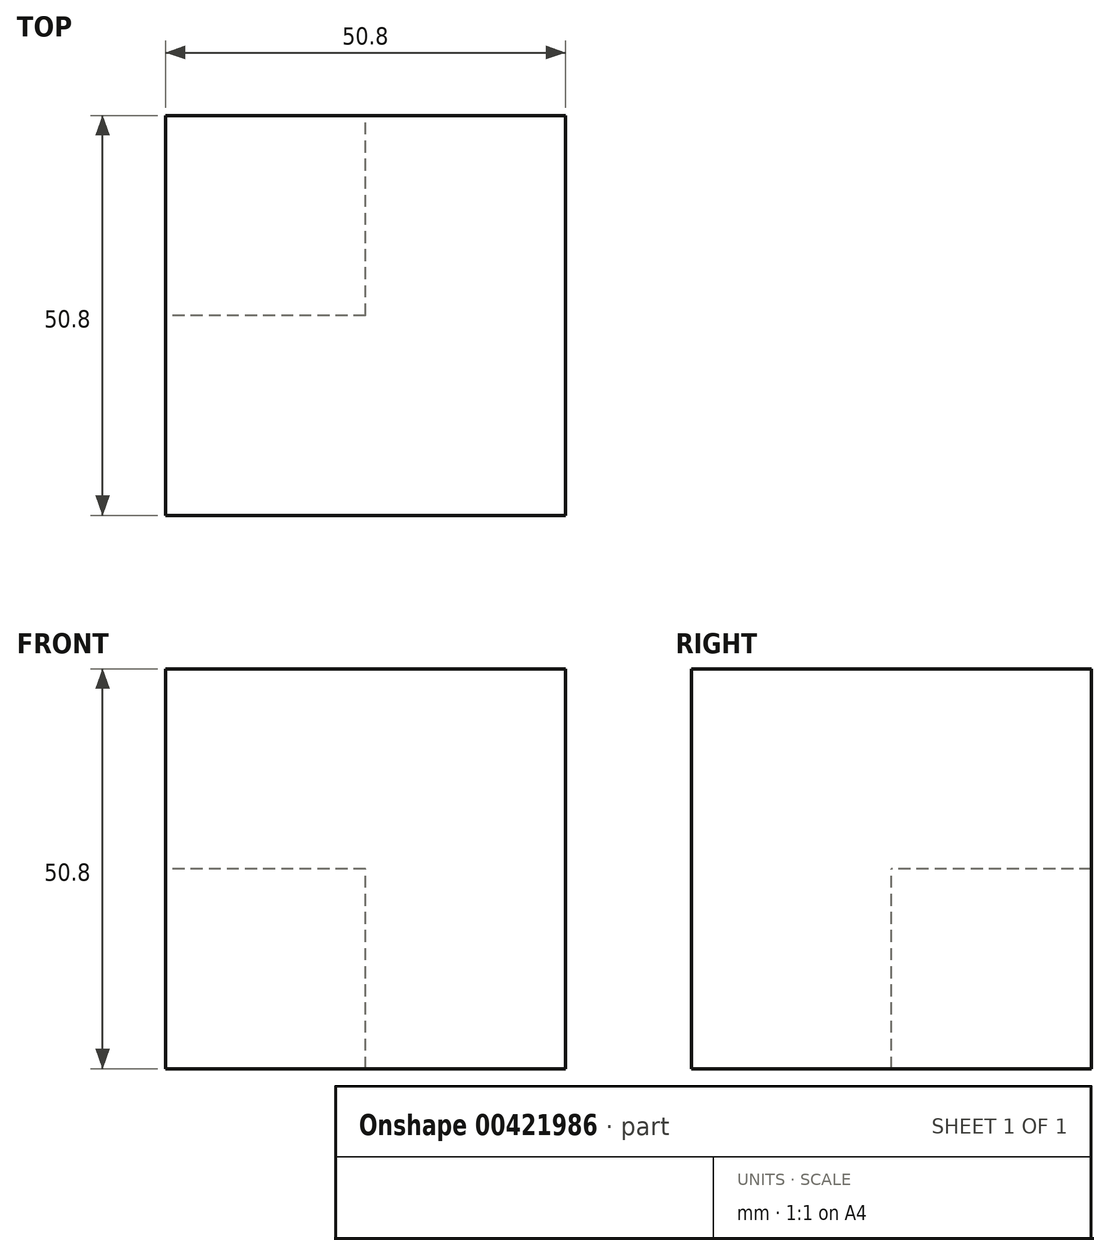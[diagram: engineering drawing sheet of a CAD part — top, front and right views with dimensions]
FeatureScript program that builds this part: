
annotation { "Feature Type Name" : "Feature", "Feature Type Description" : "" }
export const myFeature = defineFeature(function(context is Context, id is Id, definition is map)
    precondition{}
    {
        {
            var Q0;
            Q0=qCreatedBy(makeId("Front.planeOp"),FACE);
            var sketch = newSketch(context, id + "F0", { "sketchPlane" : qUnion([Q0])});
            skLineSegment(sketch, "E0.bottom", {"start": v(0, 0) * mm, "end": v(-50.8, 0) * mm});
            skLineSegment(sketch, "E0.top", {"start": v(0, 50.8) * mm, "end": v(-50.8, 50.8) * mm});
            skLineSegment(sketch, "E0.left", {"start": v(0, 0) * mm, "end": v(0, 50.8) * mm});
            skLineSegment(sketch, "E0.right", {"start": v(-50.8, 0) * mm, "end": v(-50.8, 50.8) * mm});
            skSolve(sketch);
        }
        {
            var Q0;
            Q0=makeQuery(id+"F0.imprint","IMPRINT",FACE,{"disambiguationData":[TD([[makeQuery(id+"F0.imprint","IMPRINT",EDGE,{"derivedFrom":sQuery(id+"F0.wireOp",EDGE,"E0.bottom")}),-1.0]])]});
            extrude(context, id + "F1", {"entities" : qUnion([Q0]), "depth" : 50.8 * mm});
        }
        {
            var Q0;
            Q0=makeQuery(id+"F1.opExtrude","SWEPT_FACE",FACE,{"disambiguationData":[OSD([sQuery(id+"F0.wireOp",EDGE,"E0.right")])]});
            var sketch = newSketch(context, id + "F2", { "sketchPlane" : qUnion([Q0])});
            skSolve(sketch);
        }
        {
            var Q0;
            {var subQ0=sQuery(id+"F0.wireOp",EDGE,"E0.right");Q0=makeQuery(id+"F2.imprint","IMPRINT",FACE,{"disambiguationData":[TD([[makeQuery(id+"F2.imprint","IMPRINT",EDGE,{"derivedFrom":makeQuery(id+"F1.opExtrude","CAP_EDGE",EDGE,{"disambiguationData":[OSD([subQ0])],"isStart":true})}),-1.0]])]});}
            var sketch = newSketch(context, id + "F3", { "sketchPlane" : qUnion([Q0])});
            skLineSegment(sketch, "E1.bottom", {"start": v(0, 0) * mm, "end": v(25.4, 0) * mm});
            skLineSegment(sketch, "E1.top", {"start": v(0, 25.4) * mm, "end": v(25.4, 25.4) * mm});
            skLineSegment(sketch, "E1.left", {"start": v(0, 0) * mm, "end": v(0, 25.4) * mm});
            skLineSegment(sketch, "E1.right", {"start": v(25.4, 0) * mm, "end": v(25.4, 25.4) * mm});
            skSolve(sketch);
        }
        {
            var Q0;
            Q0=makeQuery(id+"F3.imprint","IMPRINT",FACE,{"disambiguationData":[TD([[makeQuery(id+"F3.imprint","IMPRINT",EDGE,{"derivedFrom":sQuery(id+"F3.wireOp",EDGE,"E1.bottom")}),-1.0]])]});
            extrude(context, id + "F4", {"entities" : qUnion([Q0]), "operationType" : NewBodyOperationType.REMOVE, "oppositeDirection" : true, "depth" : 25.4 * mm});
        }
    });
